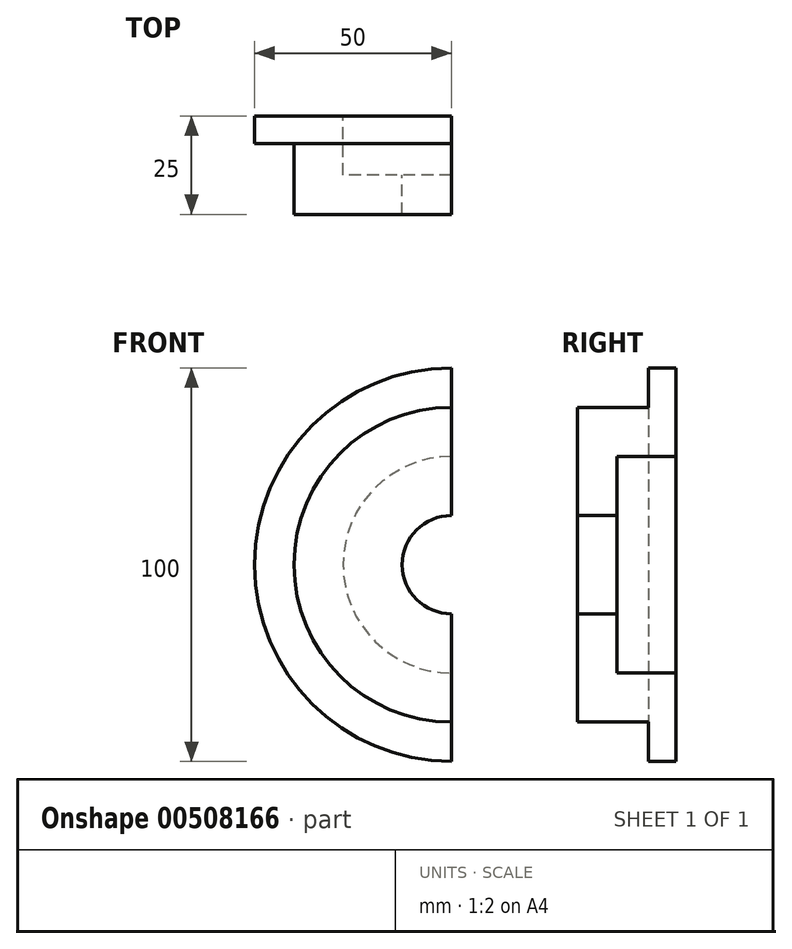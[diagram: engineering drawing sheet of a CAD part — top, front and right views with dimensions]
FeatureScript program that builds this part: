
annotation { "Feature Type Name" : "Feature", "Feature Type Description" : "" }
export const myFeature = defineFeature(function(context is Context, id is Id, definition is map)
    precondition{}
    {
        {
            var Q0;
            Q0=qCreatedBy(makeId("Front.planeOp"),FACE);
            var sketch = newSketch(context, id + "F0", { "sketchPlane" : qUnion([Q0])});
            skArc(sketch, "E0", {"start": v(0, 40) * mm, "mid": v(-40, 0) * mm, "end": v(0, -40) * mm});
            skArc(sketch, "E1", {"start": v(0, 50) * mm, "mid": v(-50, 0) * mm, "end": v(0, -50) * mm});
            skArc(sketch, "E2", {"start": v(0, 12.5) * mm, "mid": v(-12.5, 0) * mm, "end": v(0, -12.5) * mm});
            skLineSegment(sketch, "E3", {"start": v(0, 50) * mm, "end": v(0, -50) * mm});
            skArc(sketch, "E4", {"start": v(0, 27.5) * mm, "mid": v(-27.5, 0) * mm, "end": v(0, -27.5) * mm});
            skSolve(sketch);
        }
        {
            var Q0;
            {var subQ0=sQuery(id+"F0.wireOp",EDGE,"E0");Q0=makeQuery(id+"F0.imprint","IMPRINT",FACE,{"disambiguationData":[TD([[makeQuery(id+"F0.imprint","IMPRINT",EDGE,{"derivedFrom":subQ0}),1.0]])]});}
            var Q1;
            {var subQ0=sQuery(id+"F0.wireOp",EDGE,"E2");Q1=makeQuery(id+"F0.imprint","IMPRINT",FACE,{"disambiguationData":[TD([[makeQuery(id+"F0.imprint","IMPRINT",EDGE,{"derivedFrom":subQ0}),-1.0]])]});}
            extrude(context, id + "F1", {"entities" : qUnion([Q0, Q1]), "depth" : 25 * mm});
        }
        {
            var Q0;
            {var subQ0=sQuery(id+"F0.wireOp",EDGE,"E0");Q0=makeQuery(id+"F0.imprint","IMPRINT",FACE,{"disambiguationData":[TD([[makeQuery(id+"F0.imprint","IMPRINT",EDGE,{"derivedFrom":subQ0}),-1.0]])]});}
            extrude(context, id + "F2", {"entities" : qUnion([Q0]), "operationType" : NewBodyOperationType.ADD, "depth" : 7 * mm});
        }
        {
            var Q0;
            {var subQ0=sQuery(id+"F0.wireOp",EDGE,"E2");Q0=makeQuery(id+"F0.imprint","IMPRINT",FACE,{"disambiguationData":[TD([[makeQuery(id+"F0.imprint","IMPRINT",EDGE,{"derivedFrom":subQ0}),-1.0]])]});}
            extrude(context, id + "F3", {"entities" : qUnion([Q0]), "operationType" : NewBodyOperationType.REMOVE, "depth" : 15 * mm});
        }
    });
